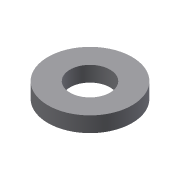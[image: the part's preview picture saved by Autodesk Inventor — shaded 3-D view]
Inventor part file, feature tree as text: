
AUTODESK INVENTOR PART (.ipt)
format: ipt  version: 2016 (Build 200138000, 138)  size: 74,752 bytes
history: native  units: mm
features: extrude x1, sketch x1
ambient origin geometry x8: Origin, YZ Plane, XZ Plane, XY Plane, X Axis, Y Axis, Z Axis, Center Point
bodies: Solid1 (feature_tree)
feature tree (2):
  extrude  "Extrusion1"  Depth=1.5mm
  sketch  "Sketch1"  dims[d0=8.2mm d1=3.9mm d2=1.5mm d3=0.0mm]
